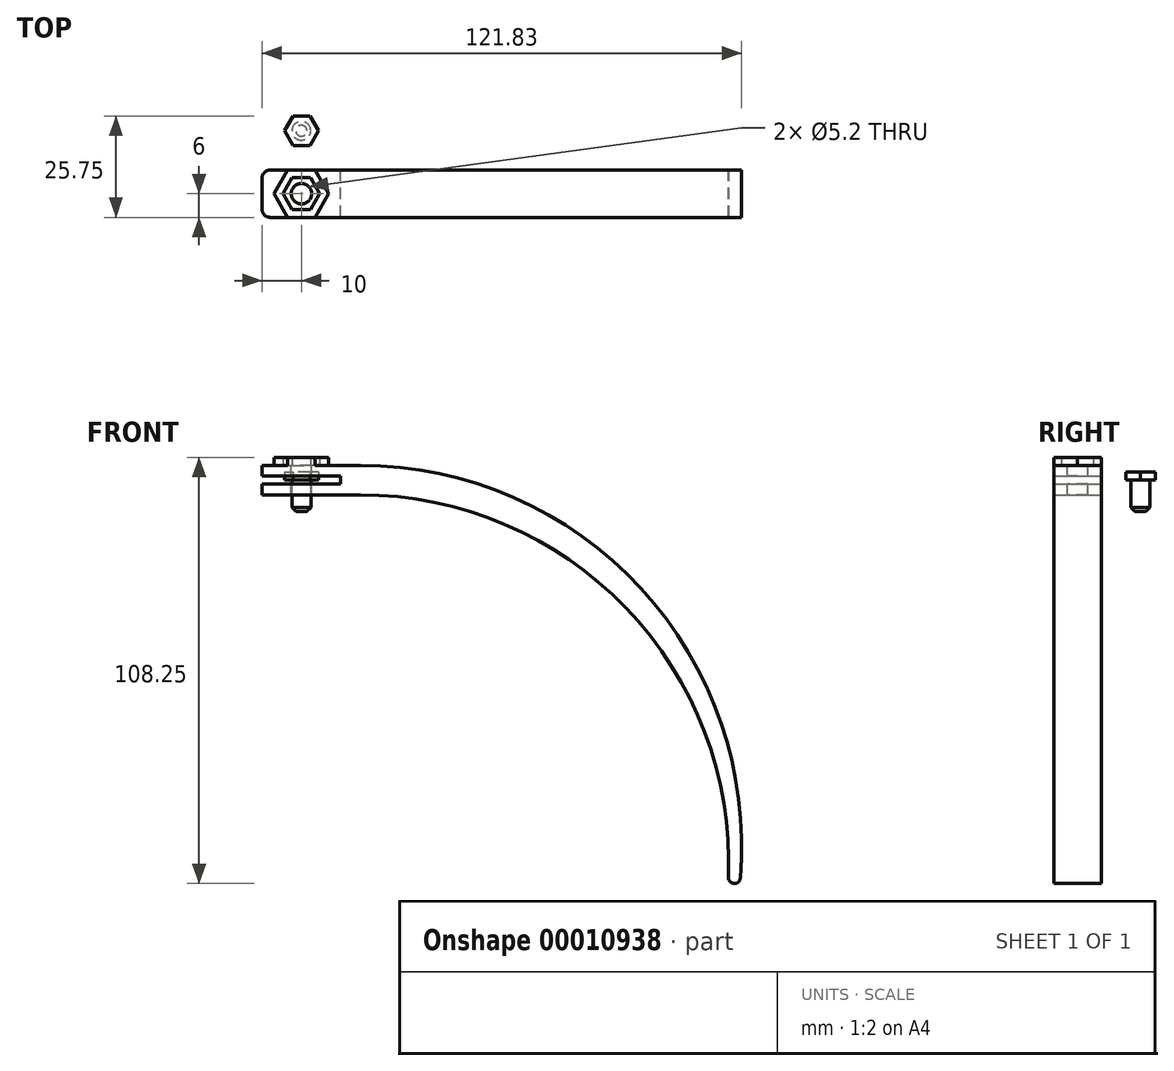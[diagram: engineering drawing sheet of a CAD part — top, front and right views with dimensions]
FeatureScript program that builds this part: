
annotation { "Feature Type Name" : "Feature", "Feature Type Description" : "" }
export const myFeature = defineFeature(function(context is Context, id is Id, definition is map)
    precondition{}
    {
        {
            var Q0;
            Q0=qCreatedBy(makeId("Front.planeOp"),FACE);
            var sketch = newSketch(context, id + "F0", { "sketchPlane" : qUnion([Q0])});
            skLineSegment(sketch, "E0.rect.bottom", {"start": v(10, -1) * mm, "end": v(-10, -1) * mm});
            skLineSegment(sketch, "E0.rect.top", {"start": v(10, 1) * mm, "end": v(-10, 1) * mm});
            skLineSegment(sketch, "E0.rect.left", {"start": v(10, -1) * mm, "end": v(10, 1) * mm});
            skLineSegment(sketch, "E0.rect.right", {"start": v(-10, -1) * mm, "end": v(-10, 1) * mm});
            skPoint(sketch, "E0.rect.middle", {"position": v(0, 0) * mm});
            skLineSegment(sketch, "E1.rect.bottom", {"start": v(10, -3.75) * mm, "end": v(-10, -3.75) * mm});
            skLineSegment(sketch, "E1.rect.top", {"start": v(10, 3.75) * mm, "end": v(-10, 3.75) * mm});
            skLineSegment(sketch, "E1.rect.left", {"start": v(10, -3.75) * mm, "end": v(10, 3.75) * mm, "construction": true});
            skLineSegment(sketch, "E1.rect.right", {"start": v(-10, -3.75) * mm, "end": v(-10, 3.75) * mm});
            skLineSegment(sketch, "E2.bottom", {"start": v(10, -3.75) * mm, "end": v(15, -3.75) * mm});
            skLineSegment(sketch, "E2.top", {"start": v(10, 3.75) * mm, "end": v(15, 3.75) * mm});
            skLineSegment(sketch, "E2.right", {"start": v(15, -3.75) * mm, "end": v(15, 3.75) * mm, "construction": true});
            skLineSegment(sketch, "E3", {"start": v(10, -1) * mm, "end": v(10, -101) * mm, "construction": true});
            skLineSegment(sketch, "E4", {"start": v(10, -101) * mm, "end": v(110, -101) * mm, "construction": true});
            skCircle(sketch, "E5", {"center": v(110, -101) * mm, "radius": 1.5 * mm});
            skArc(sketch, "E6", {"start": v(111.5, -101.12) * mm, "mid": v(86.26, -27.52) * mm, "end": v(15, 3.75) * mm});
            skArc(sketch, "E7", {"start": v(108.5, -100.94) * mm, "mid": v(82.43, -32.45) * mm, "end": v(15, -3.75) * mm});
            skSolve(sketch);
        }
        {
            var Q0;
            {var subQ5=sQuery(id+"F0.wireOp",EDGE,"E0.rect.bottom");Q0=makeQuery(id+"F0.imprint","IMPRINT",FACE,{"disambiguationData":[TD([[makeQuery(id+"F0.imprint","IMPRINT",EDGE,{"derivedFrom":subQ5}),1.0]])]});}
            var Q1;
            {var subQ0=sQuery(id+"F0.wireOp",EDGE,"E5");var subQ2=makeQuery(id+"F0.imprint","INTERSECT",VERTEX,{"derivedFrom":[subQ0,sQuery(id+"F0.wireOp",EDGE,"E6")]});Q1=makeQuery(id+"F0.imprint","IMPRINT",FACE,{"disambiguationData":[TD([[makeQuery(id+"F0.imprint","IMPRINT",EDGE,{"disambiguationData":[TD([[subQ2,1.0]])],"derivedFrom":subQ0}),1.0]])]});}
            extrude(context, id + "F1", {"entities" : qUnion([Q0, Q1]), "depth" : 12 * mm});
        }
        {
            var Q0;
            Q0=makeQuery(id+"F1.opExtrude","SWEPT_FACE",FACE,{"disambiguationData":[OSD([sQuery(id+"F0.wireOp",EDGE,"E1.rect.top"),sQuery(id+"F0.wireOp",EDGE,"E2.top")])]});
            var sketch = newSketch(context, id + "F2", { "sketchPlane" : qUnion([Q0])});
            skPoint(sketch, "E8", {"position": v(0, -6) * mm});
            skCircle(sketch, "E9.cCircle", {"center": v(0, -6) * mm, "radius": 4.05 * mm, "construction": true});
            skLineSegment(sketch, "E9.0", {"start": v(2.34, -10.05) * mm, "end": v(-2.34, -10.05) * mm});
            skLineSegment(sketch, "E9.1", {"start": v(-2.34, -10.05) * mm, "end": v(-4.68, -6) * mm});
            skLineSegment(sketch, "E9.2", {"start": v(-4.68, -6) * mm, "end": v(-2.34, -1.95) * mm});
            skLineSegment(sketch, "E9.3", {"start": v(-2.34, -1.95) * mm, "end": v(2.34, -1.95) * mm});
            skLineSegment(sketch, "E9.4", {"start": v(2.34, -1.95) * mm, "end": v(4.68, -6) * mm});
            skLineSegment(sketch, "E9.5", {"start": v(4.68, -6) * mm, "end": v(2.34, -10.05) * mm});
            skPoint(sketch, "E9.0.midPoint", {"position": v(0, -10.05) * mm});
            skCircle(sketch, "E10.cCircle", {"center": v(0, -6) * mm, "radius": 6 * mm, "construction": true});
            skLineSegment(sketch, "E10.0", {"start": v(3.46, -12) * mm, "end": v(-3.46, -12) * mm});
            skLineSegment(sketch, "E10.1", {"start": v(-3.46, -12) * mm, "end": v(-6.93, -6) * mm});
            skLineSegment(sketch, "E10.2", {"start": v(-6.93, -6) * mm, "end": v(-3.46, 0) * mm});
            skLineSegment(sketch, "E10.3", {"start": v(-3.46, 0) * mm, "end": v(3.46, 0) * mm});
            skLineSegment(sketch, "E10.4", {"start": v(3.46, 0) * mm, "end": v(6.93, -6) * mm});
            skLineSegment(sketch, "E10.5", {"start": v(6.93, -6) * mm, "end": v(3.46, -12) * mm});
            skPoint(sketch, "E10.0.midPoint", {"position": v(0, -12) * mm});
            skSolve(sketch);
        }
        {
            var Q0;
            Q0=sQuery(id+"F2.wireOp",VERTEX,"E8");
            var Q1;
            Q1=makeQuery(id+"F1.opExtrude","SWEPT_BODY",BODY,{"disambiguationData":[OSD([sQuery(id+"F0.wireOp",EDGE,"E0.rect.bottom"),sQuery(id+"F0.wireOp",EDGE,"E0.rect.top"),sQuery(id+"F0.wireOp",EDGE,"E0.rect.left"),sQuery(id+"F0.wireOp",EDGE,"E1.rect.bottom"),sQuery(id+"F0.wireOp",EDGE,"E1.rect.top"),sQuery(id+"F0.wireOp",EDGE,"E1.rect.right"),sQuery(id+"F0.wireOp",EDGE,"E2.bottom"),sQuery(id+"F0.wireOp",EDGE,"E2.top"),sQuery(id+"F0.wireOp",EDGE,"E5"),sQuery(id+"F0.wireOp",EDGE,"E6"),sQuery(id+"F0.wireOp",EDGE,"E7")])]});
            hole(context, id + "F3", {"style" : HoleStyle.SIMPLE, "holeDiameter" : 5.2 * mm, "endStyle" : HoleEndStyle.THROUGH, "locations" : qUnion([Q0]), "scope" : qUnion([Q1])});
        }
        {
            var Q0;
            Q0=makeQuery(id+"F2.imprint","IMPRINT",FACE,{"disambiguationData":[TD([[makeQuery(id+"F2.imprint","IMPRINT",EDGE,{"derivedFrom":sQuery(id+"F2.wireOp",EDGE,"E9.0")}),1.0]])]});
            extrude(context, id + "F4", {"entities" : qUnion([Q0]), "operationType" : NewBodyOperationType.ADD, "depth" : 2 * mm});
        }
        {
            var Q0;
            Q0=makeQuery(id+"F4.opExtrude","CAP_EDGE",EDGE,{"disambiguationData":[OSD([sQuery(id+"F2.wireOp",EDGE,"E10.1")])],"isStart":true});
            var Q1;
            Q1=makeQuery(id+"F4.opExtrude","CAP_EDGE",EDGE,{"disambiguationData":[OSD([sQuery(id+"F2.wireOp",EDGE,"E10.2")])],"isStart":true});
            var Q2;
            Q2=makeQuery(id+"F4.opExtrude","CAP_EDGE",EDGE,{"disambiguationData":[OSD([sQuery(id+"F2.wireOp",EDGE,"E10.5")])],"isStart":true});
            var Q3;
            Q3=makeQuery(id+"F4.opExtrude","CAP_EDGE",EDGE,{"disambiguationData":[OSD([sQuery(id+"F2.wireOp",EDGE,"E10.4")])],"isStart":true});
            var Q4;
            Q4=makeQuery(id+"F1.opExtrude","SWEPT_EDGE",EDGE,{"disambiguationData":[OSD([sQuery(id+"F0.wireOp",EDGE,"E2.top"),sQuery(id+"F0.wireOp",EDGE,"E6")])]});
            var Q5;
            {var subQ0=sQuery(id+"F0.wireOp",EDGE,"E1.rect.right");Q5=makeQuery(id+"F1.opExtrude","CAP_EDGE",EDGE,{"disambiguationData":[OSD([subQ0]),TDD([makeQuery(id+"F0.imprint","IMPRINT",EDGE,{"disambiguationData":[TD([[makeQuery(id+"F0.imprint","INTERSECT",VERTEX,{"derivedFrom":[sQuery(id+"F0.wireOp",EDGE,"E0.rect.top"),subQ0]}),-1.0]])],"derivedFrom":subQ0})])],"isStart":false});}
            var Q6;
            {var subQ0=sQuery(id+"F0.wireOp",EDGE,"E1.rect.right");Q6=makeQuery(id+"F1.opExtrude","CAP_EDGE",EDGE,{"disambiguationData":[OSD([subQ0]),TDD([makeQuery(id+"F0.imprint","IMPRINT",EDGE,{"disambiguationData":[TD([[makeQuery(id+"F0.imprint","INTERSECT",VERTEX,{"derivedFrom":[sQuery(id+"F0.wireOp",EDGE,"E0.rect.bottom"),subQ0]}),1.0]])],"derivedFrom":subQ0})])],"isStart":false});}
            var Q7;
            {var subQ0=sQuery(id+"F0.wireOp",EDGE,"E1.rect.right");Q7=makeQuery(id+"F1.opExtrude","CAP_EDGE",EDGE,{"disambiguationData":[OSD([subQ0]),TDD([makeQuery(id+"F0.imprint","IMPRINT",EDGE,{"disambiguationData":[TD([[makeQuery(id+"F0.imprint","INTERSECT",VERTEX,{"derivedFrom":[sQuery(id+"F0.wireOp",EDGE,"E0.rect.bottom"),subQ0]}),1.0]])],"derivedFrom":subQ0})])],"isStart":true});}
            var Q8;
            {var subQ0=sQuery(id+"F0.wireOp",EDGE,"E1.rect.right");Q8=makeQuery(id+"F1.opExtrude","CAP_EDGE",EDGE,{"disambiguationData":[OSD([subQ0]),TDD([makeQuery(id+"F0.imprint","IMPRINT",EDGE,{"disambiguationData":[TD([[makeQuery(id+"F0.imprint","INTERSECT",VERTEX,{"derivedFrom":[sQuery(id+"F0.wireOp",EDGE,"E0.rect.top"),subQ0]}),-1.0]])],"derivedFrom":subQ0})])],"isStart":true});}
            fillet(context, id + "F5", {"entities" : qUnion([Q0, Q1, Q2, Q3, Q4, Q5, Q6, Q7, Q8]), "radius" : 2 * mm, "tangentPropagation" : true, "allowEdgeOverflow" : false});
        }
        {
            var Q0;
            Q0=qCreatedBy(makeId("Top.planeOp"),FACE);
            var sketch = newSketch(context, id + "F6", { "sketchPlane" : qUnion([Q0])});
            skLineSegment(sketch, "E11", {"start": v(0, 0) * mm, "end": v(0, 10) * mm, "construction": true});
            skCircle(sketch, "E12.cCircle", {"center": v(0, 10) * mm, "radius": 3.75 * mm, "construction": true});
            skLineSegment(sketch, "E12.0", {"start": v(2.17, 6.25) * mm, "end": v(-2.17, 6.25) * mm});
            skLineSegment(sketch, "E12.1", {"start": v(-2.17, 6.25) * mm, "end": v(-4.33, 10) * mm});
            skLineSegment(sketch, "E12.2", {"start": v(-4.33, 10) * mm, "end": v(-2.17, 13.75) * mm});
            skLineSegment(sketch, "E12.3", {"start": v(-2.17, 13.75) * mm, "end": v(2.17, 13.75) * mm});
            skLineSegment(sketch, "E12.4", {"start": v(2.17, 13.75) * mm, "end": v(4.33, 10) * mm});
            skLineSegment(sketch, "E12.5", {"start": v(4.33, 10) * mm, "end": v(2.17, 6.25) * mm});
            skPoint(sketch, "E12.0.midPoint", {"position": v(0, 6.25) * mm});
            skCircle(sketch, "E13", {"center": v(0, 10) * mm, "radius": 2.4 * mm});
            skSolve(sketch);
        }
        {
            var Q0;
            Q0=makeQuery(id+"F6.imprint","IMPRINT",FACE,{"disambiguationData":[TD([[makeQuery(id+"F6.imprint","IMPRINT",EDGE,{"derivedFrom":sQuery(id+"F6.wireOp",EDGE,"E12.0")}),-1.0]])]});
            var Q1;
            Q1=makeQuery(id+"F6.imprint","IMPRINT",FACE,{"disambiguationData":[TD([[makeQuery(id+"F6.imprint","IMPRINT",EDGE,{"derivedFrom":sQuery(id+"F6.wireOp",EDGE,"E13")}),1.0]])]});
            extrude(context, id + "F7", {"entities" : qUnion([Q0, Q1]), "depth" : 2 * mm});
        }
        {
            var Q0;
            Q0=makeQuery(id+"F6.imprint","IMPRINT",FACE,{"disambiguationData":[TD([[makeQuery(id+"F6.imprint","IMPRINT",EDGE,{"derivedFrom":sQuery(id+"F6.wireOp",EDGE,"E13")}),1.0]])]});
            extrude(context, id + "F8", {"entities" : qUnion([Q0]), "operationType" : NewBodyOperationType.ADD, "oppositeDirection" : true, "depth" : 8 * mm});
        }
        {
            var Q0;
            Q0=makeQuery(id+"F8.opExtrude","CAP_EDGE",EDGE,{"disambiguationData":[OSD([sQuery(id+"F6.wireOp",EDGE,"E13")])],"isStart":false});
            chamfer(context, id + "F9", {"entities" : qUnion([Q0]), "width" : 1 * mm, "tangentPropagation" : true});
        }
    });
